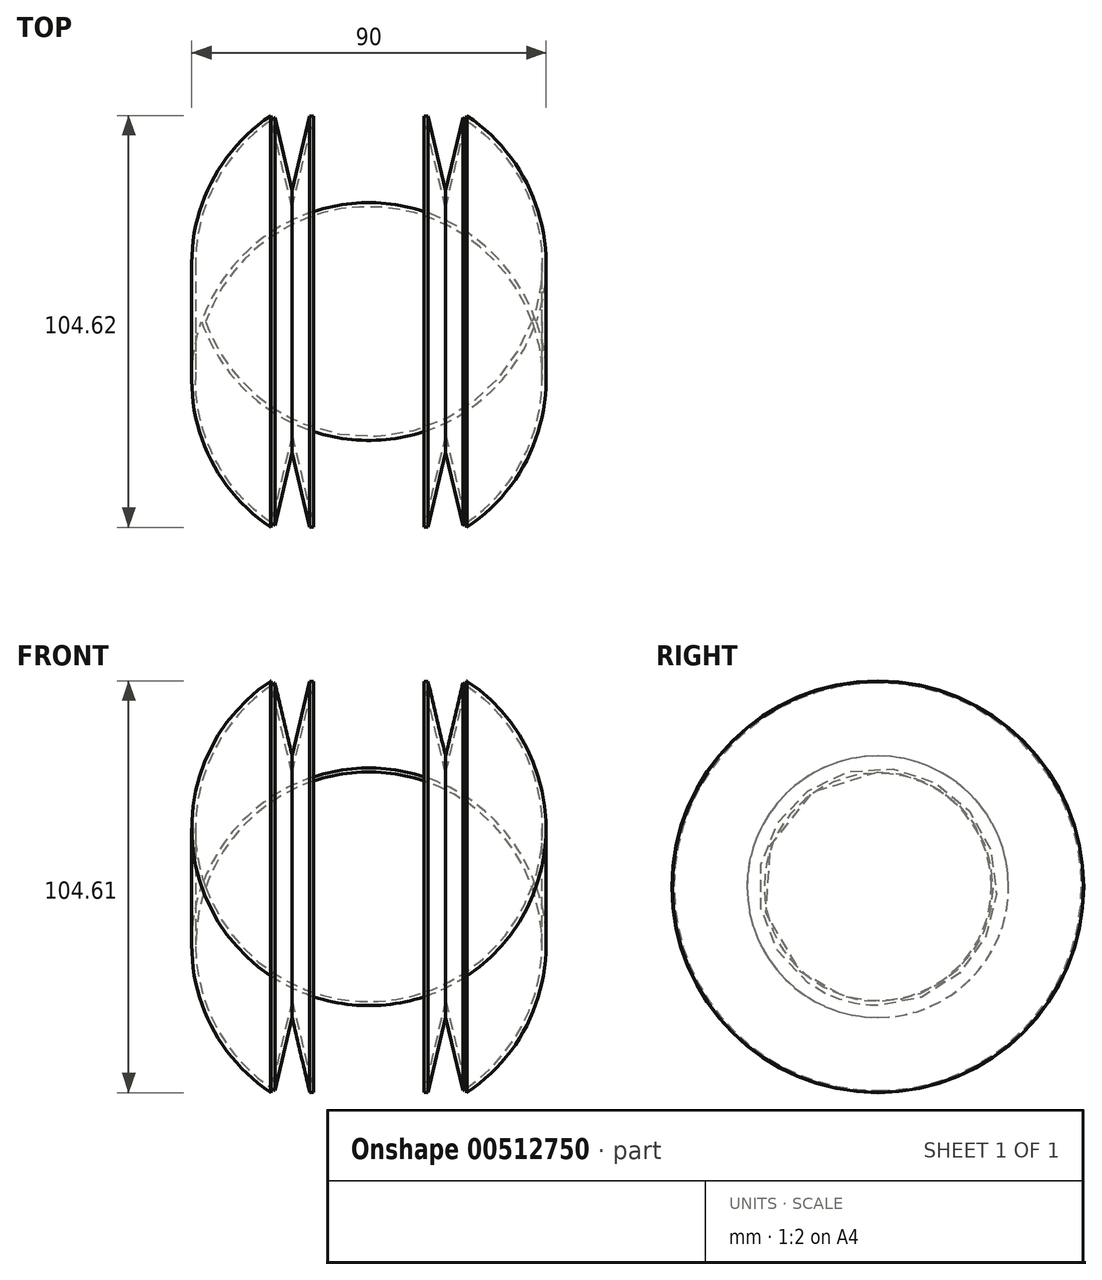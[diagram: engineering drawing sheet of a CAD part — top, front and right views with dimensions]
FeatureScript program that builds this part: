
annotation { "Feature Type Name" : "Feature", "Feature Type Description" : "" }
export const myFeature = defineFeature(function(context is Context, id is Id, definition is map)
    precondition{}
    {
        {
            var Q0;
            Q0=qCreatedBy(makeId("Front.planeOp"),FACE);
            var sketch = newSketch(context, id + "F0", { "sketchPlane" : qUnion([Q0])});
            skLineSegment(sketch, "E0", {"start": v(-25, 0) * mm, "end": v(0, 16.58) * mm});
            skLineSegment(sketch, "E1", {"start": v(0, 16.58) * mm, "end": v(25, 0) * mm});
            skLineSegment(sketch, "E2", {"start": v(25, 0) * mm, "end": v(19.5, -23.36) * mm});
            skLineSegment(sketch, "E3", {"start": v(19.5, -23.36) * mm, "end": v(14, 0) * mm});
            skLineSegment(sketch, "E4", {"start": v(14, 0) * mm, "end": v(-14, 0) * mm});
            skLineSegment(sketch, "E5", {"start": v(-14, 0) * mm, "end": v(-19.5, -23.36) * mm});
            skLineSegment(sketch, "E6", {"start": v(-19.5, -23.36) * mm, "end": v(-25, 0) * mm});
            skSolve(sketch);
        }
        {
            var Q0;
            Q0=qCreatedBy(makeId("Front.planeOp"),FACE);
            var sketch = newSketch(context, id + "F1", { "sketchPlane" : qUnion([Q0])});
            skLineSegment(sketch, "E7", {"start": v(0, 0) * mm, "end": v(0, -52.22) * mm});
            skLineSegment(sketch, "E8", {"start": v(0, -52.22) * mm, "end": v(-15.71, -52.22) * mm});
            skLineSegment(sketch, "E9", {"start": v(0, -52.22) * mm, "end": v(17.9, -52.22) * mm});
            skSolve(sketch);
        }
        {
            var Q0;
            Q0 = qSketchRegion(id + "F0", true);
            var Q1;
            Q1=sQuery(id+"F1.wireOp",EDGE,"E9");
            revolve(context, id + "F2", {"entities" : qUnion([Q0]), "axis" : qUnion([Q1]), "revolveType" : RevolveType.FULL});
        }
        {
            var Q0;
            Q0=makeQuery(id+"F2.opRevolve","SWEPT_EDGE",EDGE,{"disambiguationData":[OSD([sQuery(id+"F0.wireOp",EDGE,"E0"),sQuery(id+"F0.wireOp",EDGE,"E1")])]});
            fillet(context, id + "F3", {"entities" : qUnion([Q0]), "radius" : 45 * mm, "tangentPropagation" : true, "allowEdgeOverflow" : false});
        }
        {
            var Q0;
            Q0=makeQuery(id+"F2.opRevolve","SWEPT_FACE",FACE,{"disambiguationData":[OSD([sQuery(id+"F0.wireOp",EDGE,"E4")])]});
            shell(context, id + "F4", {"entities" : qUnion([Q0]), "thickness" : 1 * mm});
        }
    });
